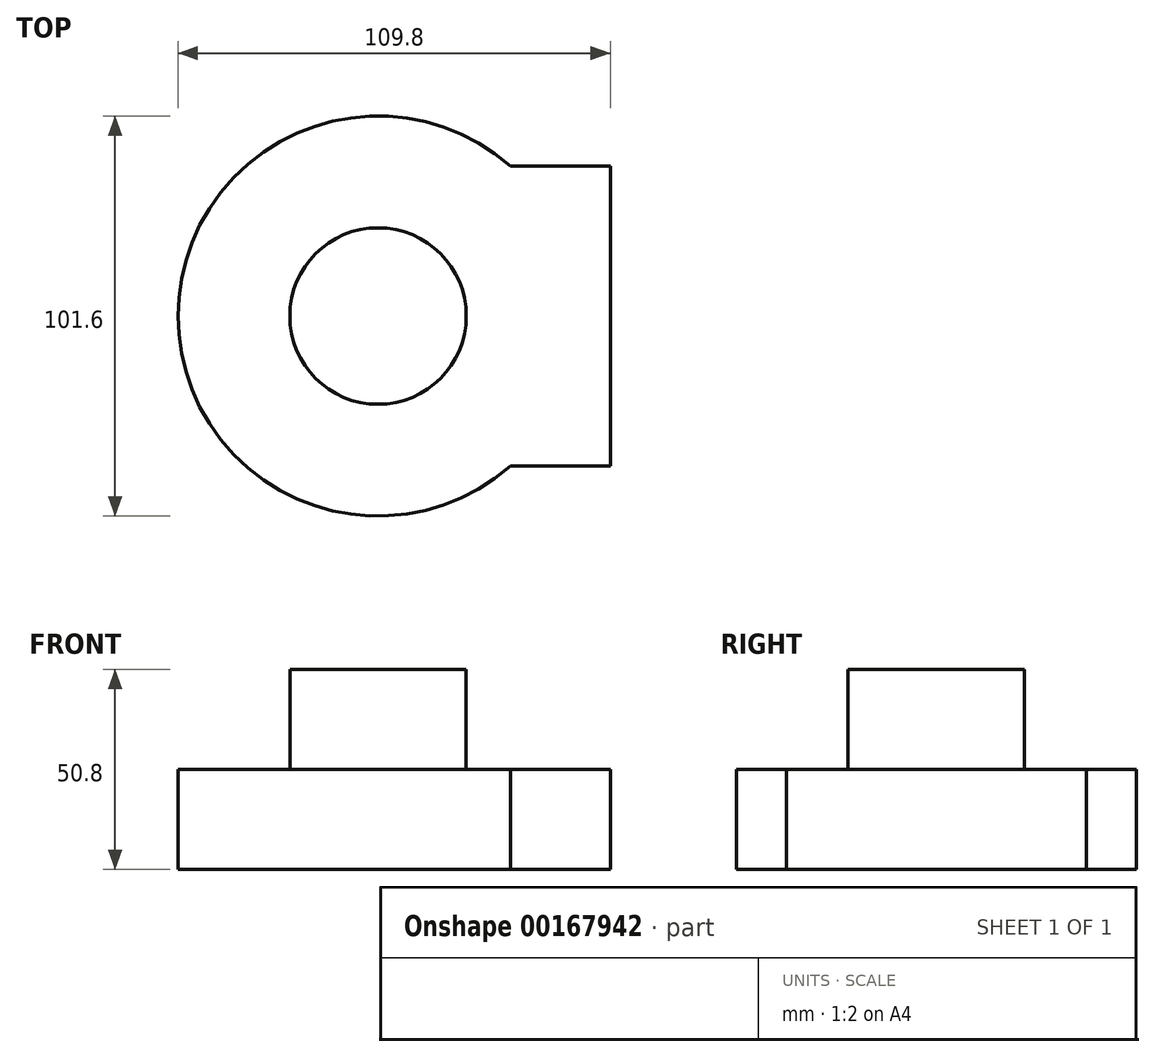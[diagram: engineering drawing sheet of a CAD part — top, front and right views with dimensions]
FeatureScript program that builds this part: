
annotation { "Feature Type Name" : "Feature", "Feature Type Description" : "" }
export const myFeature = defineFeature(function(context is Context, id is Id, definition is map)
    precondition{}
    {
        {
            var Q0;
            Q0=qCreatedBy(makeId("Top.planeOp"),FACE);
            var sketch = newSketch(context, id + "F0", { "sketchPlane" : qUnion([Q0])});
            skArc(sketch, "E0", {"start": v(33.6, 38.1) * mm, "mid": v(-50.8, 0) * mm, "end": v(33.6, -38.1) * mm});
            skLineSegment(sketch, "E1.bottom", {"start": v(33.6, -38.1) * mm, "end": v(59, -38.1) * mm});
            skLineSegment(sketch, "E1.top", {"start": v(33.6, 38.1) * mm, "end": v(59, 38.1) * mm});
            skLineSegment(sketch, "E1.right", {"start": v(59, -38.1) * mm, "end": v(59, 38.1) * mm});
            skLineSegment(sketch, "E2", {"start": v(0, 0) * mm, "end": v(59, 0) * mm, "construction": true});
            skSolve(sketch);
        }
        {
            var Q0;
            Q0 = qSketchRegion(id + "F0", true);
            extrude(context, id + "F1", {"entities" : qUnion([Q0]), "depth" : 25.4 * mm});
        }
        {
            var Q0;
            Q0=makeQuery(id+"F1.opExtrude","CAP_FACE",FACE,{"disambiguationData":[OSD([sQuery(id+"F0.wireOp",EDGE,"E0"),sQuery(id+"F0.wireOp",EDGE,"E1.bottom"),sQuery(id+"F0.wireOp",EDGE,"E1.top"),sQuery(id+"F0.wireOp",EDGE,"E1.right")])],"isStart":false});
            var sketch = newSketch(context, id + "F2", { "sketchPlane" : qUnion([Q0])});
            skCircle(sketch, "E3", {"center": v(0, 0) * mm, "radius": 22.41 * mm});
            skSolve(sketch);
        }
        {
            var Q0;
            Q0 = qSketchRegion(id + "F2", true);
            extrude(context, id + "F3", {"entities" : qUnion([Q0]), "operationType" : NewBodyOperationType.ADD, "depth" : 25.4 * mm});
        }
    });
